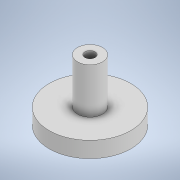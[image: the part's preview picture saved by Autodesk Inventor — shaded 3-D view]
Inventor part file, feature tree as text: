
AUTODESK INVENTOR PART (.ipt)
format: ipt  version: 2022 (Build 260153000, 153)  size: 108,544 bytes
history: native  units: mm
features: extrude x3, sketch x3
ambient origin geometry x8: Origin, YZ Plane, XZ Plane, XY Plane, X Axis, Y Axis, Z Axis, Center Point
bodies: Solid1 (feature_tree)
feature tree (6):
  extrude  "Extrusion1"  Depth=3.5mm TaperAngle=0.0deg
  extrude  "Extrusion2"  Depth=10.0mm TaperAngle=0.0deg
  extrude  "Extrusion3"  Depth=3.5mm TaperAngle=0.0deg
  sketch  "Sketch1"  dims[d0=18.0mm d1=3.5mm d2=0.0mm]
  sketch  "Sketch2"  dims[d3=5.5mm d4=10.0mm d5=0.0mm]
  sketch  "Sketch3"  dims[d6=2.25mm d7=3.5mm d8=0.0mm]
